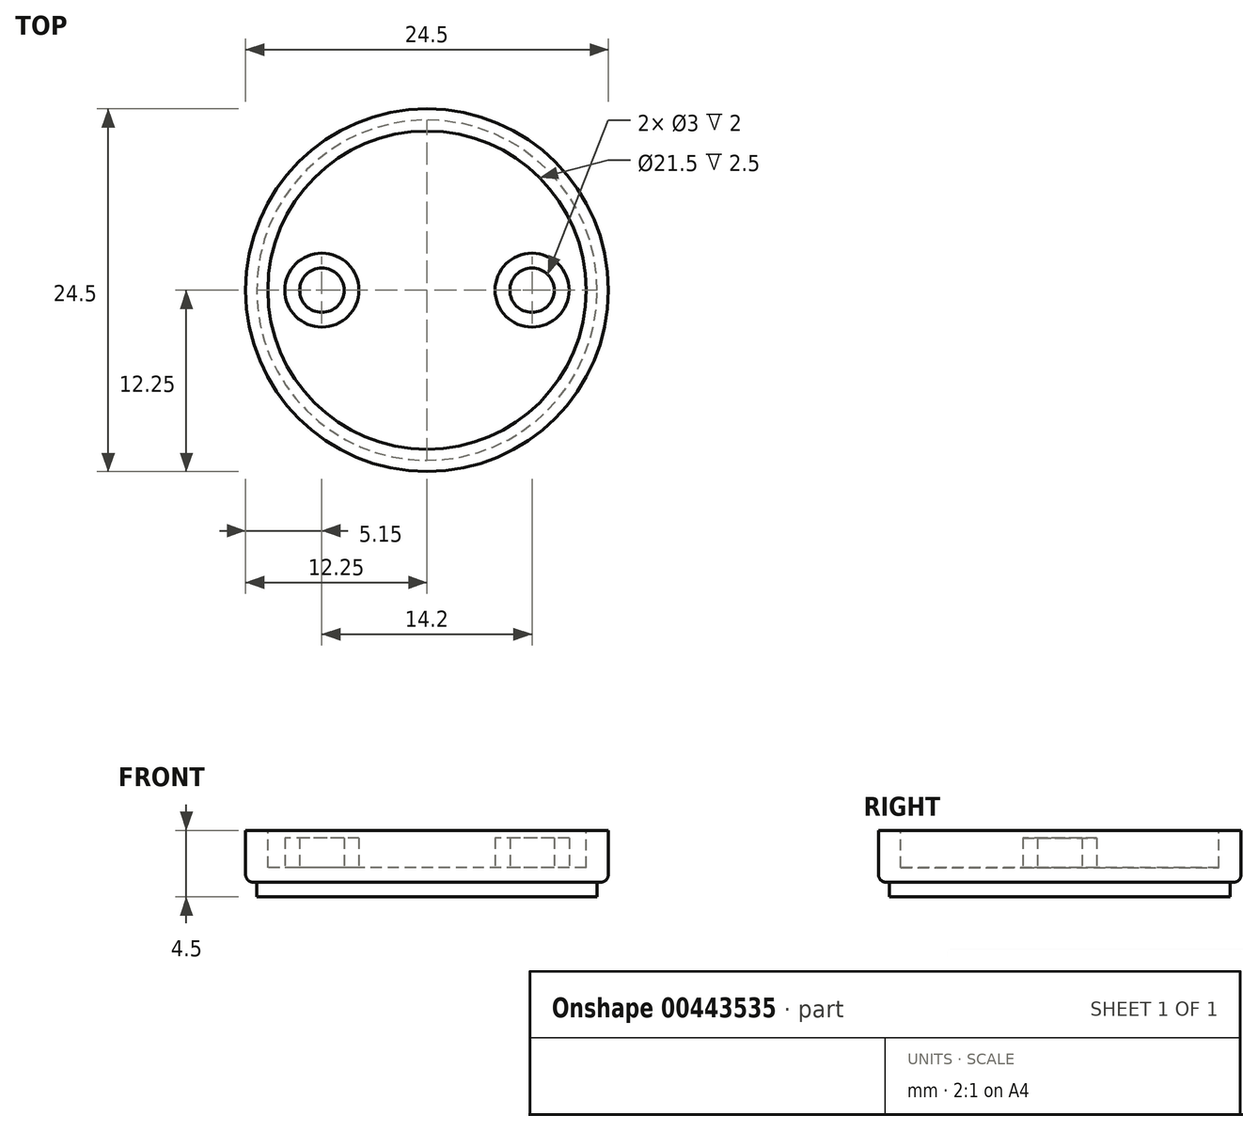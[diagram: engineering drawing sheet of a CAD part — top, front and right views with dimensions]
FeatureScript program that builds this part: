
annotation { "Feature Type Name" : "Feature", "Feature Type Description" : "" }
export const myFeature = defineFeature(function(context is Context, id is Id, definition is map)
    precondition{}
    {
        {
            var Q0;
            Q0=qCreatedBy(makeId("Top.planeOp"),FACE);
            var sketch = newSketch(context, id + "F0", { "sketchPlane" : qUnion([Q0])});
            skCircle(sketch, "E0", {"center": v(0, 0) * mm, "radius": 11.5 * mm});
            skSolve(sketch);
        }
        {
            var Q0;
            Q0=makeQuery(id+"F0.imprint","IMPRINT",FACE,{"disambiguationData":[TD([[makeQuery(id+"F0.imprint","IMPRINT",EDGE,{"derivedFrom":sQuery(id+"F0.wireOp",EDGE,"E0")}),1.0]])]});
            extrude(context, id + "F1", {"entities" : qUnion([Q0]), "depth" : 1 * mm});
        }
        {
            var Q0;
            Q0=makeQuery(id+"F1.opExtrude","CAP_FACE",FACE,{"disambiguationData":[OSD([sQuery(id+"F0.wireOp",EDGE,"E0")])],"isStart":false});
            var sketch = newSketch(context, id + "F2", { "sketchPlane" : qUnion([Q0])});
            skCircle(sketch, "E1", {"center": v(0, 0) * mm, "radius": 12.25 * mm});
            skSolve(sketch);
        }
        {
            var Q0;
            Q0 = qSketchRegion(id + "F2", true);
            extrude(context, id + "F3", {"entities" : qUnion([Q0]), "operationType" : NewBodyOperationType.ADD, "depth" : 3.5 * mm});
        }
        {
            var Q0;
            Q0=makeQuery(id+"F3.opExtrude","CAP_FACE",FACE,{"disambiguationData":[OSD([sQuery(id+"F2.wireOp",EDGE,"E1")])],"isStart":false});
            var sketch = newSketch(context, id + "F4", { "sketchPlane" : qUnion([Q0])});
            skCircle(sketch, "E2", {"center": v(0, 0) * mm, "radius": 10.75 * mm});
            skSolve(sketch);
        }
        {
            var Q0;
            Q0=makeQuery(id+"F4.imprint","IMPRINT",FACE,{"disambiguationData":[TD([[makeQuery(id+"F4.imprint","IMPRINT",EDGE,{"derivedFrom":sQuery(id+"F4.wireOp",EDGE,"E2")}),1.0]])]});
            extrude(context, id + "F5", {"entities" : qUnion([Q0]), "operationType" : NewBodyOperationType.REMOVE, "oppositeDirection" : true, "depth" : 2.5 * mm});
        }
        {
            var Q0;
            Q0=makeQuery(id+"F3.opExtrude","CAP_EDGE",EDGE,{"disambiguationData":[OSD([sQuery(id+"F2.wireOp",EDGE,"E1")])],"isStart":true});
            fillet(context, id + "F6", {"entities" : qUnion([Q0]), "radius" : 0.5 * mm, "tangentPropagation" : true, "allowEdgeOverflow" : false});
        }
        {
            var Q0;
            Q0=makeQuery(id+"F5.boolean.opBoolean","COPY",FACE,{"derivedFrom":makeQuery(id+"F5.opExtrude","CAP_FACE",FACE,{"disambiguationData":[OSD([sQuery(id+"F4.wireOp",EDGE,"E2")])],"isStart":false})});
            var sketch = newSketch(context, id + "F7", { "sketchPlane" : qUnion([Q0])});
            skCircle(sketch, "E3", {"center": v(7.1, 0) * mm, "radius": 1.5 * mm});
            skCircle(sketch, "E4", {"center": v(-7.1, 0) * mm, "radius": 1.5 * mm});
            skLineSegment(sketch, "E5.bottom", {"start": v(-8.6, 1.5) * mm, "end": v(8.6, 1.5) * mm, "construction": true});
            skLineSegment(sketch, "E5.top", {"start": v(-8.6, -1.5) * mm, "end": v(8.6, -1.5) * mm, "construction": true});
            skLineSegment(sketch, "E5.left", {"start": v(-8.6, 1.5) * mm, "end": v(-8.6, -1.5) * mm, "construction": true});
            skLineSegment(sketch, "E5.right", {"start": v(8.6, 1.5) * mm, "end": v(8.6, -1.5) * mm, "construction": true});
            skLineSegment(sketch, "E6", {"start": v(0, -1.5) * mm, "end": v(0, 1.5) * mm, "construction": true});
            skCircle(sketch, "E7", {"center": v(-7.1, 0) * mm, "radius": 2.5 * mm});
            skCircle(sketch, "E8", {"center": v(7.1, 0) * mm, "radius": 2.5 * mm});
            skSolve(sketch);
        }
        {
            var Q0;
            Q0 = qSketchRegion(id + "F7", true);
            extrude(context, id + "F8", {"entities" : qUnion([Q0]), "operationType" : NewBodyOperationType.ADD, "depth" : 2 * mm});
        }
    });
